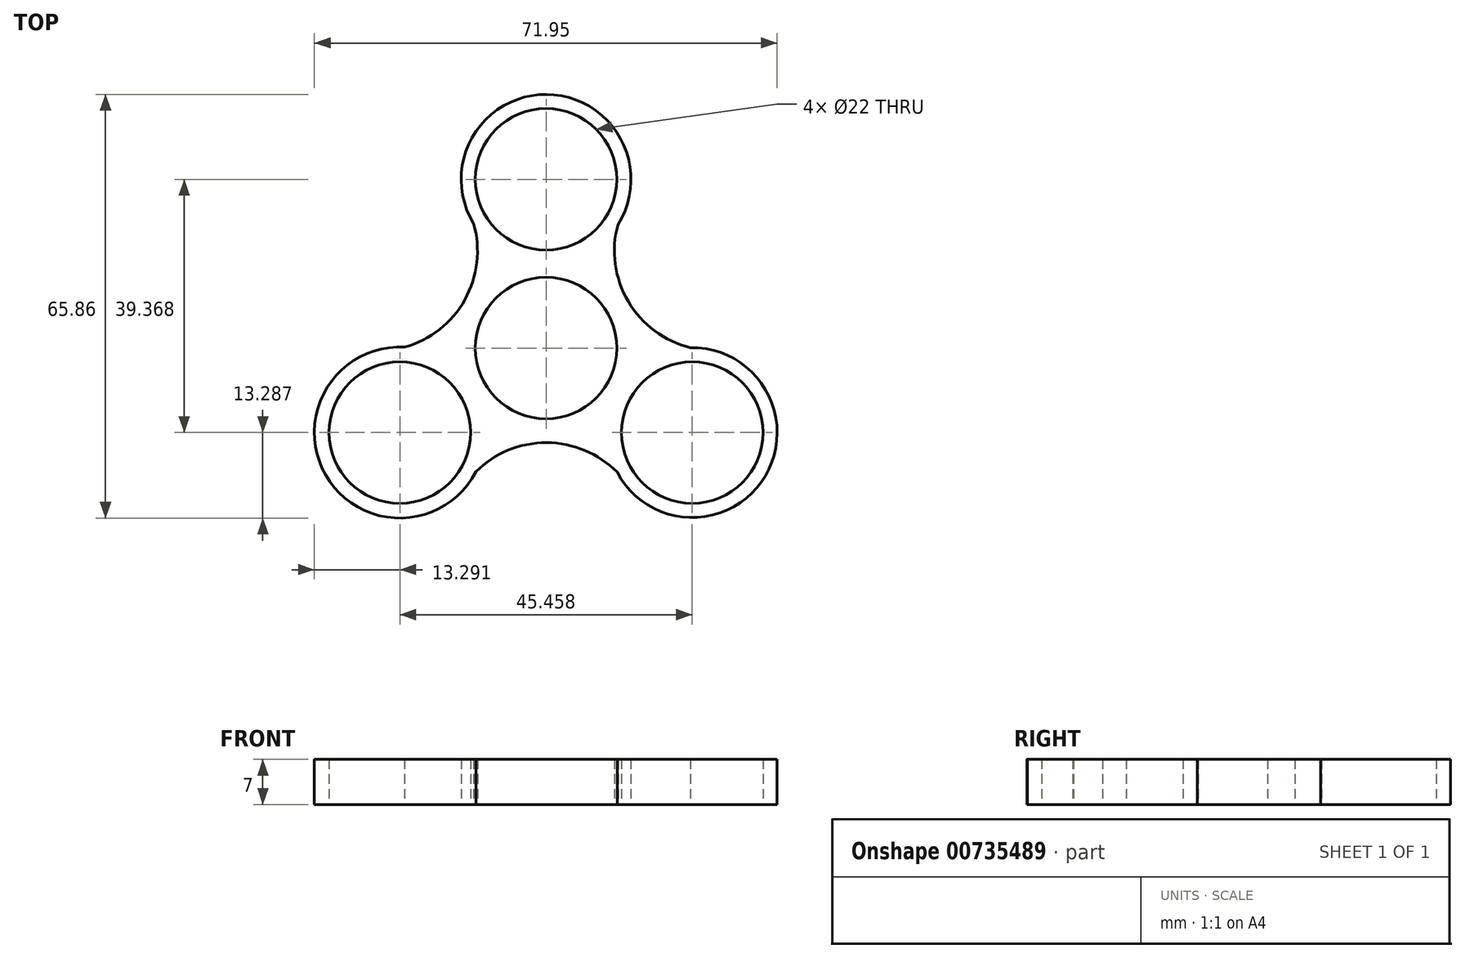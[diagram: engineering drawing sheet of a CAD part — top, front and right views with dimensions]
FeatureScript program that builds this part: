
annotation { "Feature Type Name" : "Feature", "Feature Type Description" : "" }
export const myFeature = defineFeature(function(context is Context, id is Id, definition is map)
    precondition{}
    {
        {
            var Q0;
            Q0=qCreatedBy(makeId("Top.planeOp"),FACE);
            var sketch = newSketch(context, id + "F0", { "sketchPlane" : qUnion([Q0])});
            skCircle(sketch, "E0", {"center": v(0, 0) * mm, "radius": 11 * mm});
            skCircle(sketch, "E1", {"center": v(0, 26.24) * mm, "radius": 11 * mm});
            skCircle(sketch, "E2.1.1", {"center": v(-22.73, -13.13) * mm, "radius": 11 * mm});
            skCircle(sketch, "E2.2.1", {"center": v(22.73, -13.13) * mm, "radius": 11 * mm});
            skPoint(sketch, "E2.center", {"position": v(0, -0.01) * mm});
            skArc(sketch, "E3", {"start": v(11.42, 20.03) * mm, "mid": v(12.84, 7.15) * mm, "end": v(23.54, -0.16) * mm});
            skArc(sketch, "E4.1.0", {"start": v(-23.06, -0.12) * mm, "mid": v(-12.6, 7.54) * mm, "end": v(-11.63, 20.46) * mm});
            skArc(sketch, "E4.2.0", {"start": v(11.63, -19.9) * mm, "mid": v(-0.23, -14.7) * mm, "end": v(-11.9, -20.3) * mm});
            skArc(sketch, "E5", {"start": v(-21.98, 0.14) * mm, "mid": v(-34.26, -19.74) * mm, "end": v(-10.9, -19.21) * mm});
            skArc(sketch, "E6", {"start": v(11.17, 19.2) * mm, "mid": v(0.1, 39.43) * mm, "end": v(-11.27, 19.36) * mm});
            skArc(sketch, "E7", {"start": v(11.05, -19.28) * mm, "mid": v(34.1, -19.84) * mm, "end": v(22.46, 0.06) * mm});
            skSolve(sketch);
        }
        {
            var Q0;
            Q0=makeQuery(id+"F0.imprint","IMPRINT",FACE,{"disambiguationData":[TD([[makeQuery(id+"F0.imprint","IMPRINT",EDGE,{"derivedFrom":sQuery(id+"F0.wireOp",EDGE,"E0")}),-1.0]])]});
            extrude(context, id + "F1", {"entities" : qUnion([Q0]), "depth" : 7 * mm, "offsetDistance" : 25 * mm});
        }
    });
